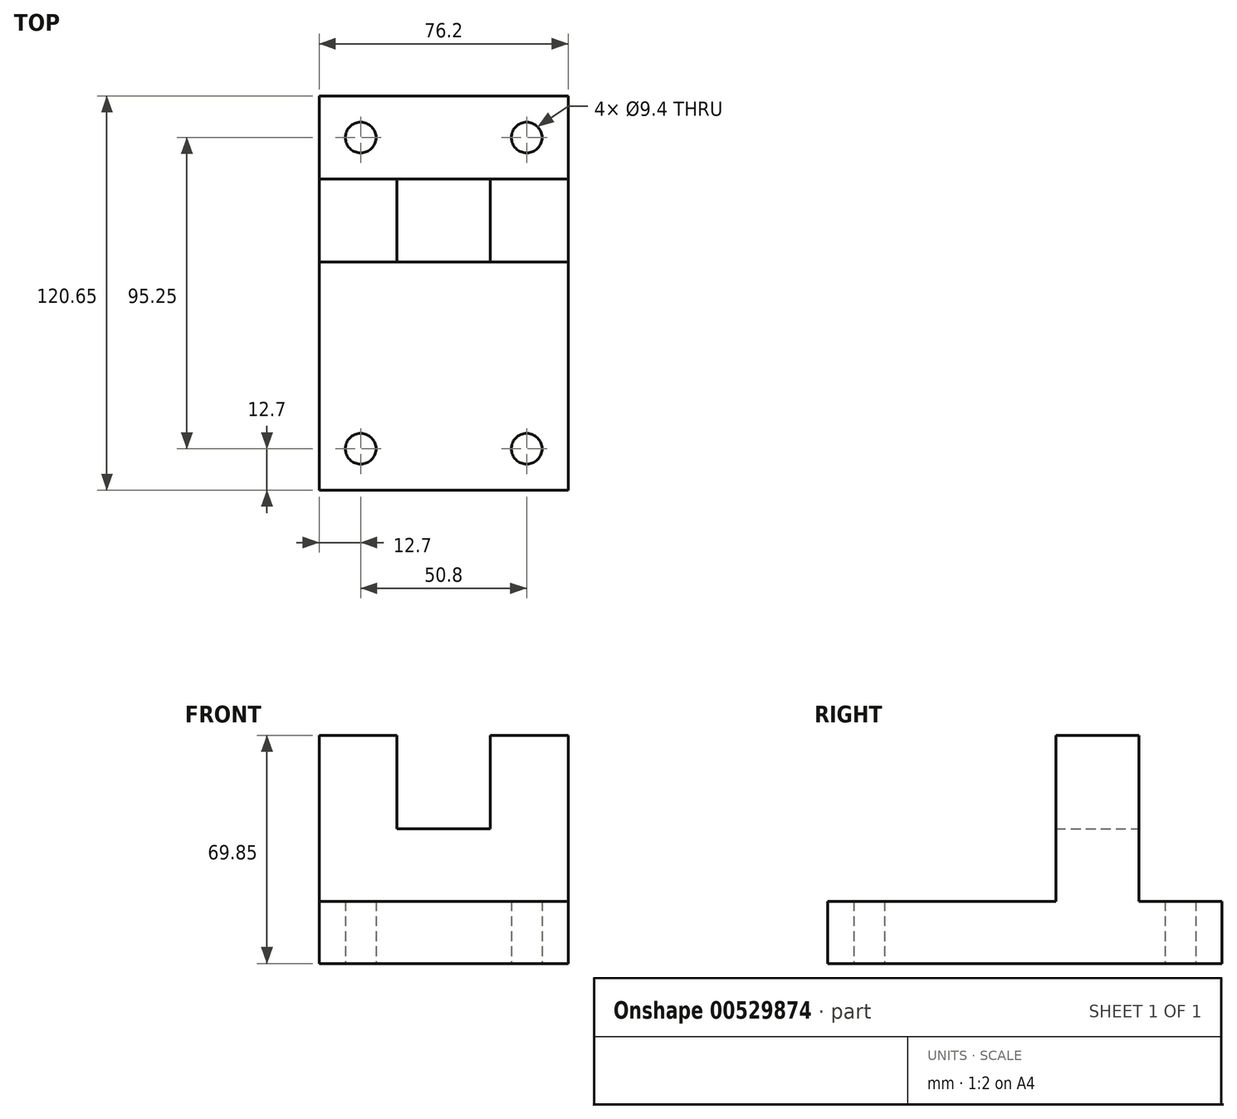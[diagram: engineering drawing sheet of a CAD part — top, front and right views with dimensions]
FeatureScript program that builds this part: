
annotation { "Feature Type Name" : "Feature", "Feature Type Description" : "" }
export const myFeature = defineFeature(function(context is Context, id is Id, definition is map)
    precondition{}
    {
        {
            var Q0;
            Q0=qCreatedBy(makeId("Front.planeOp"),FACE);
            var sketch = newSketch(context, id + "F0", { "sketchPlane" : qUnion([Q0])});
            skLineSegment(sketch, "E0.bottom", {"start": v(38.1, -34.92) * mm, "end": v(-38.1, -34.93) * mm});
            skLineSegment(sketch, "E0.left", {"start": v(38.1, -34.92) * mm, "end": v(38.1, 34.93) * mm});
            skLineSegment(sketch, "E0.right", {"start": v(-38.1, -34.93) * mm, "end": v(-38.1, 34.92) * mm});
            skPoint(sketch, "E0.middle", {"position": v(0, 0) * mm});
            skLineSegment(sketch, "E1", {"start": v(-38.1, 34.92) * mm, "end": v(-14.27, 34.92) * mm});
            skLineSegment(sketch, "E2", {"start": v(14.3, 34.92) * mm, "end": v(38.1, 34.93) * mm});
            skLineSegment(sketch, "E3", {"start": v(14.3, 34.92) * mm, "end": v(14.3, 6.35) * mm});
            skLineSegment(sketch, "E4", {"start": v(14.3, 6.35) * mm, "end": v(-14.27, 6.35) * mm});
            skLineSegment(sketch, "E5", {"start": v(-14.27, 6.35) * mm, "end": v(-14.27, 34.92) * mm});
            skSolve(sketch);
        }
        {
            var Q0;
            Q0 = qSketchRegion(id + "F0", true);
            extrude(context, id + "F1", {"entities" : qUnion([Q0]), "depth" : 25.4 * mm, "offsetDistance" : 25.4 * mm});
        }
        {
            var Q0;
            Q0=makeQuery(id+"F1.opExtrude","SWEPT_FACE",FACE,{"disambiguationData":[OSD([sQuery(id+"F0.wireOp",EDGE,"E0.bottom")])]});
            var sketch = newSketch(context, id + "F2", { "sketchPlane" : qUnion([Q0])});
            skLineSegment(sketch, "E6", {"start": v(-38.1, 25.4) * mm, "end": v(-38.1, 25.4) * mm});
            skLineSegment(sketch, "E7", {"start": v(38.1, 0) * mm, "end": v(38.1, -25.4) * mm});
            skLineSegment(sketch, "E8", {"start": v(38.1, -25.4) * mm, "end": v(-38.1, -25.4) * mm});
            skLineSegment(sketch, "E9", {"start": v(-38.1, -25.4) * mm, "end": v(-38.1, 0) * mm});
            skLineSegment(sketch, "E10", {"start": v(38.1, 25.4) * mm, "end": v(38.1, 95.25) * mm});
            skLineSegment(sketch, "E11", {"start": v(-38.1, 25.4) * mm, "end": v(-38.1, 95.25) * mm});
            skLineSegment(sketch, "E12", {"start": v(38.1, 95.25) * mm, "end": v(-38.1, 95.25) * mm});
            skLineSegment(sketch, "E13", {"start": v(38.1, 95.25) * mm, "end": v(25.4, 95.25) * mm});
            skLineSegment(sketch, "E14", {"start": v(38.1, 95.25) * mm, "end": v(38.1, 82.55) * mm});
            skCircle(sketch, "E15", {"center": v(25.4, 82.55) * mm, "radius": 4.7 * mm});
            skLineSegment(sketch, "E16", {"start": v(-38.1, 95.25) * mm, "end": v(-25.4, 95.25) * mm});
            skLineSegment(sketch, "E17", {"start": v(-38.1, 95.25) * mm, "end": v(-38.1, 82.55) * mm});
            skCircle(sketch, "E18", {"center": v(-25.4, 82.55) * mm, "radius": 4.7 * mm});
            skLineSegment(sketch, "E19", {"start": v(38.1, -25.4) * mm, "end": v(25.4, -25.4) * mm});
            skLineSegment(sketch, "E20", {"start": v(38.1, -25.4) * mm, "end": v(38.1, -12.7) * mm});
            skCircle(sketch, "E21", {"center": v(25.4, -12.7) * mm, "radius": 4.7 * mm});
            skCircle(sketch, "E22", {"center": v(-25.4, -12.7) * mm, "radius": 4.7 * mm});
            skSolve(sketch);
        }
        {
            var Q0;
            Q0=makeQuery(id+"F2.imprint","IMPRINT",FACE,{"disambiguationData":[TD([[makeQuery(id+"F2.imprint","IMPRINT",EDGE,{"derivedFrom":sQuery(id+"F2.wireOp",EDGE,"E10")}),1.0]])]});
            var Q1;
            Q1=makeQuery(id+"F2.imprint","IMPRINT",FACE,{"disambiguationData":[TD([[makeQuery(id+"F2.imprint","IMPRINT",EDGE,{"derivedFrom":sQuery(id+"F2.wireOp",EDGE,"E7")}),-1.0]])]});
            extrude(context, id + "F3", {"entities" : qUnion([Q0, Q1]), "operationType" : NewBodyOperationType.ADD, "oppositeDirection" : true, "depth" : 19.05 * mm, "offsetDistance" : 25.4 * mm});
        }
    });
